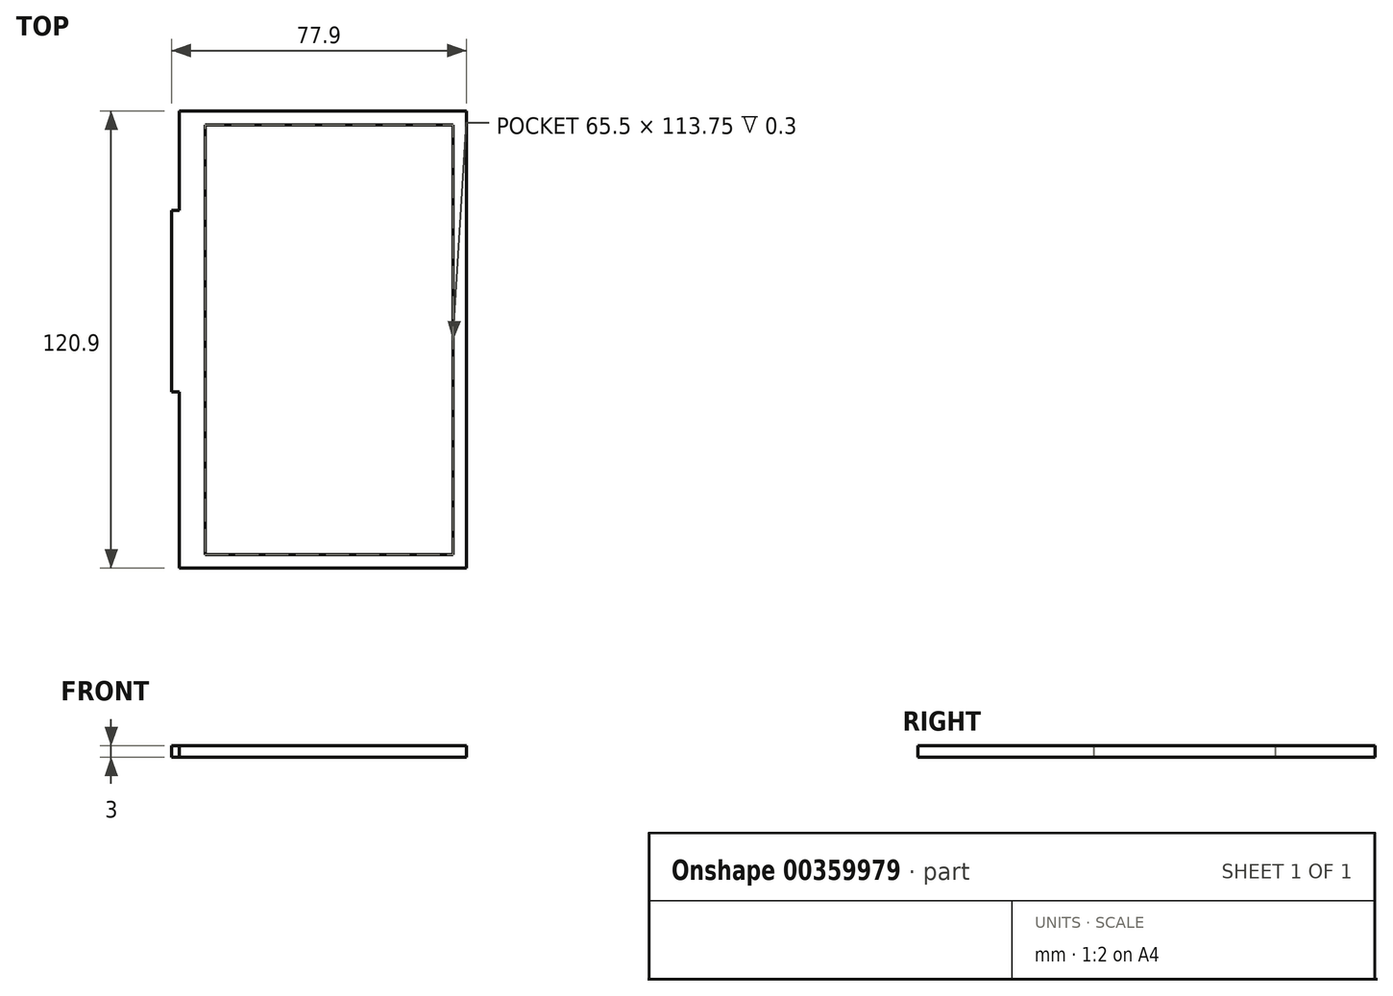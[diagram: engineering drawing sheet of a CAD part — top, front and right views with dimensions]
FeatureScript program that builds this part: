
annotation { "Feature Type Name" : "Feature", "Feature Type Description" : "" }
export const myFeature = defineFeature(function(context is Context, id is Id, definition is map)
    precondition{}
    {
        {
            var Q0;
            Q0=qCreatedBy(makeId("Top.planeOp"),FACE);
            var sketch = newSketch(context, id + "F0", { "sketchPlane" : qUnion([Q0])});
            skLineSegment(sketch, "E0.bottom", {"start": v(35.89, 60.5) * mm, "end": v(-40.01, 60.5) * mm});
            skLineSegment(sketch, "E0.top", {"start": v(35.89, -60.4) * mm, "end": v(-40.01, -60.4) * mm});
            skLineSegment(sketch, "E0.left", {"start": v(35.89, 60.5) * mm, "end": v(35.89, -60.4) * mm});
            skLineSegment(sketch, "E0.right", {"start": v(-40.01, 60.5) * mm, "end": v(-40.01, -60.4) * mm});
            skSolve(sketch);
        }
        {
            var Q0;
            Q0=makeQuery(id+"F0.imprint","IMPRINT",FACE,{"disambiguationData":[TD([[makeQuery(id+"F0.imprint","IMPRINT",EDGE,{"derivedFrom":sQuery(id+"F0.wireOp",EDGE,"E0.bottom")}),1.0]])]});
            extrude(context, id + "F1", {"entities" : qUnion([Q0]), "depth" : 3 * mm});
        }
        {
            var Q0;
            Q0=makeQuery(id+"F1.opExtrude","CAP_FACE",FACE,{"disambiguationData":[OSD([sQuery(id+"F0.wireOp",EDGE,"E0.bottom"),sQuery(id+"F0.wireOp",EDGE,"E0.top"),sQuery(id+"F0.wireOp",EDGE,"E0.left"),sQuery(id+"F0.wireOp",EDGE,"E0.right")])],"isStart":false});
            var sketch = newSketch(context, id + "F2", { "sketchPlane" : qUnion([Q0])});
            skLineSegment(sketch, "E1.bottom", {"start": v(32.39, 56.86) * mm, "end": v(-33.11, 56.86) * mm});
            skLineSegment(sketch, "E1.top", {"start": v(32.39, -56.9) * mm, "end": v(-33.11, -56.9) * mm});
            skLineSegment(sketch, "E1.left", {"start": v(32.39, 56.86) * mm, "end": v(32.39, -56.9) * mm});
            skLineSegment(sketch, "E1.right", {"start": v(-33.11, 56.86) * mm, "end": v(-33.11, -56.9) * mm});
            skSolve(sketch);
        }
        {
            var Q0;
            Q0=makeQuery(id+"F2.imprint","IMPRINT",FACE,{"disambiguationData":[TD([[makeQuery(id+"F2.imprint","IMPRINT",EDGE,{"derivedFrom":sQuery(id+"F2.wireOp",EDGE,"E1.bottom")}),1.0]])]});
            extrude(context, id + "F3", {"entities" : qUnion([Q0]), "operationType" : NewBodyOperationType.REMOVE, "oppositeDirection" : true, "depth" : .3 * mm});
        }
        {
            var Q0;
            Q0=makeQuery(id+"F1.opExtrude","SWEPT_FACE",FACE,{"disambiguationData":[OSD([sQuery(id+"F0.wireOp",EDGE,"E0.right")])]});
            var sketch = newSketch(context, id + "F4", { "sketchPlane" : qUnion([Q0])});
            skLineSegment(sketch, "E2.bottom", {"start": v(-34.18, 0) * mm, "end": v(13.82, 0) * mm});
            skLineSegment(sketch, "E2.top", {"start": v(-34.18, 3) * mm, "end": v(13.82, 3) * mm});
            skLineSegment(sketch, "E2.left", {"start": v(-34.18, 0) * mm, "end": v(-34.18, 3) * mm});
            skLineSegment(sketch, "E2.right", {"start": v(13.82, 0) * mm, "end": v(13.82, 3) * mm});
            skSolve(sketch);
        }
        {
            var Q0;
            Q0=makeQuery(id+"F4.imprint","IMPRINT",FACE,{"disambiguationData":[TD([[makeQuery(id+"F4.imprint","IMPRINT",EDGE,{"derivedFrom":sQuery(id+"F4.wireOp",EDGE,"E2.bottom")}),1.0]])]});
            extrude(context, id + "F5", {"entities" : qUnion([Q0]), "operationType" : NewBodyOperationType.ADD, "depth" : 2 * mm});
        }
    });
